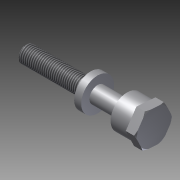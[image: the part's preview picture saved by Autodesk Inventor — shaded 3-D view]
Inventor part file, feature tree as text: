
AUTODESK INVENTOR PART (.ipt)
format: ipt  version: 2015 (Build 190159000, 159)  size: 162,304 bytes
history: native  units: mm (DEFAULTED — no unit token found)
features: sketch x3, revolve x2, chamfer x1, extrude x1, other x1, plane x1, thread x1
ambient origin geometry x8: Origin, YZ Plane, XZ Plane, XY Plane, X Axis, Y Axis, Z Axis, Center Point
bodies: Solid1 (feature_tree)
feature tree (10):
  revolve  "Revolution1"  [1 undecoded]
  chamfer  "Chamfer1"  Distance=173.0375mm
  extrude  "Extrusion1"  Depth=36.5125mm
  other  "Work Axis1"
  plane  "Work Plane1"
  revolve  "Revolution2"  [1 undecoded]
  thread  "Thread1"  [1 undecoded]
  sketch  "Sketch1"  dims[d0=11.1125mm d1=22.225mm]
  sketch  "Sketch2"  dims[d2=11.1125mm]
  sketch  "Sketch3"  dims[d3=9.525mm d4=173.0375mm d5=36.5125mm d6=39.6875mm d7=6.35mm d8=9.525mm d9=90.0deg d10=1.5875mm d11=1.5875mm d12=44.45mm d13=12.7mm d14=0.0mm d15=0.0mm d16=30.0deg d17=90.0deg d18=25.4mm d19=0.0mm d20=45.0deg]
note: 3 required parameter values undecoded (feature->parameter linkage not recoverable at this tier; creation-order binding heuristic only, values carry confidence <= 0.55)